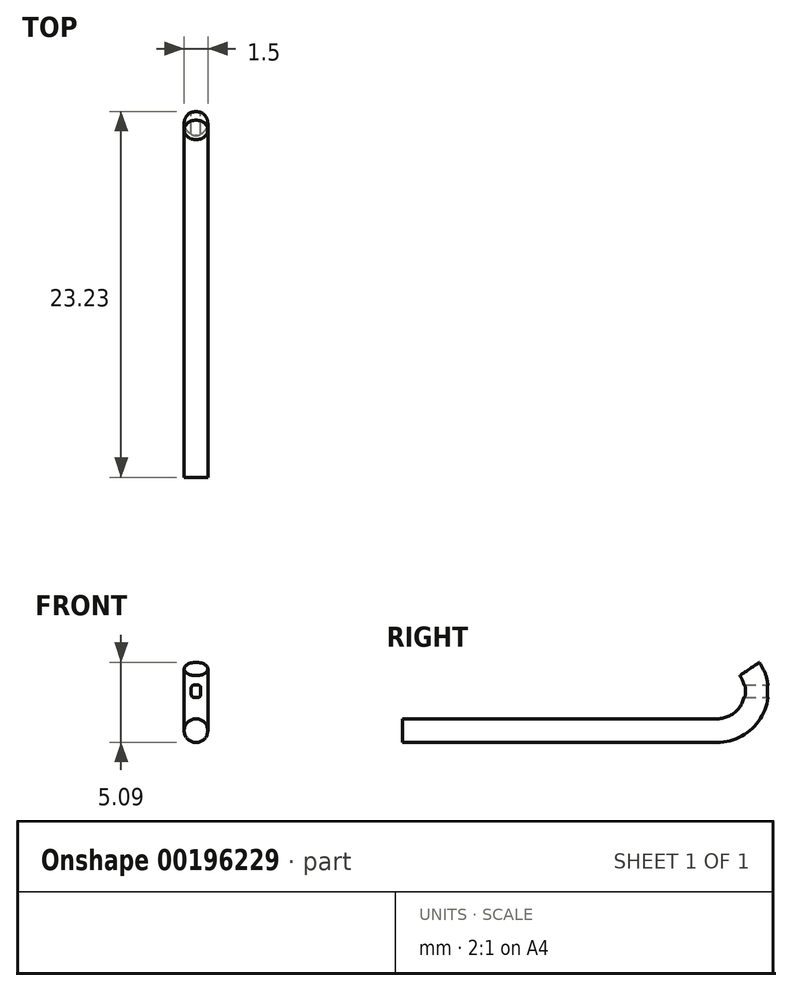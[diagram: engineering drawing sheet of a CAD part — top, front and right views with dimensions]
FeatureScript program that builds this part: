
annotation { "Feature Type Name" : "Feature", "Feature Type Description" : "" }
export const myFeature = defineFeature(function(context is Context, id is Id, definition is map)
    precondition{}
    {
        {
            var Q0;
            Q0=qCreatedBy(makeId("Right.planeOp"),FACE);
            var sketch = newSketch(context, id + "F0", { "sketchPlane" : qUnion([Q0])});
            skLineSegment(sketch, "E0", {"start": v(-20, 0) * mm, "end": v(0, 0) * mm});
            skArc(sketch, "E1", {"start": v(0, 0) * mm, "mid": v(2.21, 1.33) * mm, "end": v(2.06, 3.91) * mm});
            skLineSegment(sketch, "E2", {"start": v(0, 2.5) * mm, "end": v(8.68, 8.45) * mm, "construction": true});
            skSolve(sketch);
        }
        {
            var Q0;
            Q0=sQuery(id+"F0.wireOp",VERTEX,"E0.start");
            var Q1;
            Q1=sQuery(id+"F0.wireOp",EDGE,"E0");
            cPlane(context, id + "F1", {"entities" : qUnion([Q0, Q1]), "cplaneType" : CPlaneType.LINE_POINT, "offset" : 25 * mm, "width" : 150 * mm, "height" : 150 * mm});
        }
        {
            var Q0;
            Q0=qCreatedBy(id+"F1.planeOp",FACE);
            var sketch = newSketch(context, id + "F2", { "sketchPlane" : qUnion([Q0])});
            skCircle(sketch, "E3", {"center": v(0, 0) * mm, "radius": 0.75 * mm});
            skSolve(sketch);
        }
        {
            var Q0;
            Q0=makeQuery(id+"F2.imprint","IMPRINT",FACE,{"disambiguationData":[TD([[makeQuery(id+"F2.imprint","IMPRINT",EDGE,{"derivedFrom":sQuery(id+"F2.wireOp",EDGE,"E3")}),1.0]])]});
            var Q1;
            Q1=sQuery(id+"F0.wireOp",EDGE,"E0");
            var Q2;
            Q2=sQuery(id+"F0.wireOp",EDGE,"E1");
            sweep(context, id + "F3", {"profiles" : qUnion([Q0]), "path" : qUnion([Q1, Q2])});
        }
        {
            var Q0;
            Q0=qCreatedBy(makeId("Right.planeOp"),FACE);
            var sketch = newSketch(context, id + "F4", { "sketchPlane" : qUnion([Q0])});
            skLineSegment(sketch, "E4", {"start": v(0, 0) * mm, "end": v(0, 6.1) * mm, "construction": true});
            skLineSegment(sketch, "E5", {"start": v(0, 2.5) * mm, "end": v(4.97, 2.5) * mm});
            skSolve(sketch);
        }
        {
            var Q0;
            Q0=qCreatedBy(makeId("Front.planeOp"),FACE);
            var sketch = newSketch(context, id + "F5", { "sketchPlane" : qUnion([Q0])});
            skLineSegment(sketch, "E6.bottom", {"start": v(0.1, 2.1) * mm, "end": v(-0.1, 2.1) * mm});
            skLineSegment(sketch, "E6.top", {"start": v(0.1, 2.9) * mm, "end": v(-0.1, 2.9) * mm});
            skLineSegment(sketch, "E6.left", {"start": v(0.3, 2.3) * mm, "end": v(0.3, 2.7) * mm});
            skLineSegment(sketch, "E6.right", {"start": v(-0.3, 2.3) * mm, "end": v(-0.3, 2.7) * mm});
            skPoint(sketch, "E6.middle", {"position": v(0, 2.5) * mm});
            skPoint(sketch, "E7.visualSharp", {"position": v(-0.3, 2.9) * mm});
            skArc(sketch, "E7.filletArc", {"start": v(-0.1, 2.9) * mm, "mid": v(-0.24, 2.84) * mm, "end": v(-0.3, 2.7) * mm});
            skPoint(sketch, "E8.visualSharp", {"position": v(0.3, 2.9) * mm});
            skArc(sketch, "E8.filletArc", {"start": v(0.3, 2.7) * mm, "mid": v(0.24, 2.84) * mm, "end": v(0.1, 2.9) * mm});
            skPoint(sketch, "E9.visualSharp", {"position": v(0.3, 2.1) * mm});
            skArc(sketch, "E9.filletArc", {"start": v(0.1, 2.1) * mm, "mid": v(0.24, 2.16) * mm, "end": v(0.3, 2.3) * mm});
            skPoint(sketch, "E10.visualSharp", {"position": v(-0.3, 2.1) * mm});
            skArc(sketch, "E10.filletArc", {"start": v(-0.3, 2.3) * mm, "mid": v(-0.24, 2.16) * mm, "end": v(-0.1, 2.1) * mm});
            skSolve(sketch);
        }
        {
            var Q0;
            Q0=makeQuery(id+"F5.imprint","IMPRINT",FACE,{"disambiguationData":[TD([[makeQuery(id+"F5.imprint","IMPRINT",EDGE,{"derivedFrom":sQuery(id+"F5.wireOp",EDGE,"E6.bottom")}),-1.0]])]});
            var Q1;
            Q1 = qConstructionFilter(qBodyType(qCreatedBy(id + "F4" ,EDGE), BodyType.WIRE), ConstructionObject.NO);
            sweep(context, id + "F6", {"operationType" : NewBodyOperationType.REMOVE, "profiles" : qUnion([Q0]), "path" : qUnion([Q1])});
        }
    });
